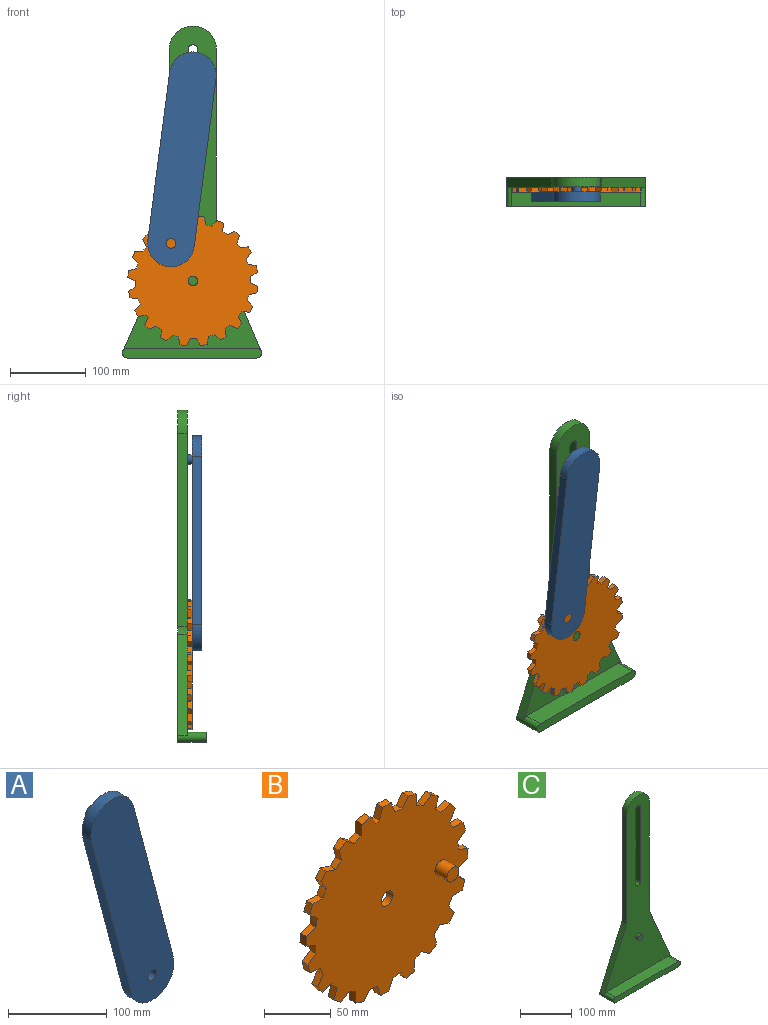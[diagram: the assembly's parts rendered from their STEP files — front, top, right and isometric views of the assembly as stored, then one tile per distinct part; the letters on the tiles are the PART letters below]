
ASSEMBLY  parts=3 mates=3
PART A: 9 faces, bbox 118.8x31.8x277.6 mm
  f0: plane 277.6x118.85mm, normal (0,-1,0), area 16641.5mm2, adj f1,f3,f4,f5,f6
  f1: plane 215.9x57.15mm, normal (0.97,0,0.26), area 2836.4mm2, adj f0,f2,f4,f5
  f2: plane 277.6x118.85mm, normal (0,1,0), area 16514.8mm2, adj f1,f3,f4,f5,f6,f8
  f3: cylinder r=6.35mm len=12.7mm, axis (0,1,0), area 506.7mm2, adj f0,f2
  f4: cylinder r=30.85mm len=60.67mm, axis (0,1,0), area 1230.8mm2, adj f0,f1,f2,f6
  f5: cylinder r=30.85mm len=60.67mm, axis (0,1,0), area 1230.8mm2, adj f0,f1,f2,f6
  f6: plane 215.9x57.15mm, normal (-0.97,0,-0.26), area 2836.4mm2, adj f0,f2,f4,f5
  f7: plane 12.7x12.7mm, normal (0,1,0), area 126.7mm2, adj f8
  f8: cylinder r=6.35mm len=19.05mm, axis (0,-1,0), area 760.1mm2, adj f2,f7
PART B: 85 faces, bbox 171.6x19.1x171.5 mm
  f0: plane 10.58x6.35mm, normal (0.05,0,1), area 67.2mm2, adj f1,f79,f80,f81
  f1: cylinder r=76.2mm len=7.18mm, axis (0,1,0), area 50.9mm2, adj f0,f2,f80,f81
  f2: plane 8.73x6.35mm, normal (0.82,0,-0.57), area 67.2mm2, adj f1,f3,f80,f81
  f3: plane 7.21x6.35mm, normal (0.81,0,0.58), area 56.2mm2, adj f2,f4,f80,f81
  f4: plane 10.2x6.35mm, normal (-0.27,0,0.96), area 67.2mm2, adj f3,f5,f80,f81
  f5: cylinder r=76.2mm len=6.35mm, axis (0,1,0), area 50.9mm2, adj f4,f6,f80,f81
  f6: plane 10.16x6.35mm, normal (0.96,0,-0.28), area 67.2mm2, adj f5,f7,f80,f81
  f7: plane 7.13x6.35mm, normal (0.59,0,0.81), area 56.2mm2, adj f6,f8,f80,f81
  f8: plane 8.81x6.35mm, normal (-0.55,0,0.83), area 67.2mm2, adj f7,f9,f80,f81
  f9: cylinder r=76.2mm len=7.13mm, axis (0,1,0), area 50.9mm2, adj f8,f10,f80,f81
  f10: plane 10.58x6.35mm, normal (1,0,0.03), area 67.2mm2, adj f9,f11,f80,f81
  f11: plane 8.41x6.35mm, normal (0.31,0,0.95), area 56.2mm2, adj f10,f12,f80,f81
  f12: plane 8.33x6.54mm, normal (-0.79,0,0.62), area 67.2mm2, adj f11,f13,f80,f81
  f13: cylinder r=76.2mm len=7.92mm, axis (0,1,0), area 50.9mm2, adj f12,f14,f80,f81
  f14: plane 9.95x6.35mm, normal (0.94,0,0.34), area 67.2mm2, adj f13,f15,f80,f81
  f15: plane 8.85x6.35mm, normal (0,0,1), area 56.2mm2, adj f14,f16,f80,f81
  f16: plane 9.95x6.35mm, normal (-0.94,0,0.34), area 67.2mm2, adj f15,f17,f80,f81
  f17: cylinder r=76.2mm len=6.35mm, axis (0,1,0), area 24.3mm2, adj f16,f18,f80,f81
  f18: plane 8.67x6.35mm, normal (0.82,0,0.57), area 67.2mm2, adj f17,f19,f80,f81
  f19: plane 8.55x6.35mm, normal (-0.26,0,0.97), area 56.2mm2, adj f18,f20,f80,f81
  f20: plane 10.55x6.35mm, normal (-1,0,0.09), area 67.2mm2, adj f19,f21,f80,f81
  f21: cylinder r=76.2mm len=7.32mm, axis (0,1,0), area 50.9mm2, adj f20,f22,f80,f81
  f22: plane 8.48x6.35mm, normal (0.6,0,0.8), area 67.2mm2, adj f21,f23,f80,f81
  f23: plane 7.41x6.35mm, normal (-0.55,0,0.84), area 56.2mm2, adj f22,f24,f80,f81
  f24: plane 10.31x6.35mm, normal (-0.97,0,-0.23), area 67.2mm2, adj f23,f25,f80,f81
  f25: cylinder r=76.2mm len=6.35mm, axis (0,1,0), area 50.9mm2, adj f24,f26,f80,f81
  f26: plane 10.03x6.35mm, normal (0.32,0,0.95), area 67.2mm2, adj f25,f27,f80,f81
  f27: plane 6.91x6.35mm, normal (-0.78,0,0.63), area 56.2mm2, adj f26,f28,f80,f81
  f28: plane 9.05x6.35mm, normal (-0.85,0,-0.52), area 67.2mm2, adj f27,f29,f80,f81
  f29: cylinder r=76.2mm len=6.97mm, axis (0,1,0), area 50.9mm2, adj f28,f30,f80,f81
  f30: plane 10.59x6.35mm, normal (0.01,0,1), area 67.2mm2, adj f29,f31,f80,f81
  f31: plane 8.29x6.35mm, normal (-0.94,0,0.35), area 56.2mm2, adj f30,f32,f80,f81
  f32: plane 8.05x6.88mm, normal (-0.65,0,-0.76), area 67.2mm2, adj f31,f33,f80,f81
  f33: cylinder r=76.2mm len=7.86mm, axis (0,1,0), area 50.9mm2, adj f32,f34,f80,f81
  f34: plane 10.09x6.35mm, normal (-0.3,0,0.95), area 67.2mm2, adj f33,f35,f80,f81
  f35: plane 8.85x6.35mm, normal (-1,0,0.04), area 56.2mm2, adj f34,f36,f80,f81
  f36: plane 9.79x6.35mm, normal (-0.38,0,-0.92), area 67.2mm2, adj f35,f37,f80,f81
  f37: cylinder r=76.2mm len=7.96mm, axis (0,1,0), area 50.9mm2, adj f36,f38,f80,f81
  f38: plane 8.59x6.35mm, normal (-0.58,0,0.81), area 67.2mm2, adj f37,f39,f80,f81
  f39: plane 8.52x6.35mm, normal (-0.96,0,-0.27), area 56.2mm2, adj f38,f40,f80,f81
  f40: plane 10.56x6.35mm, normal (-0.07,0,-1), area 67.2mm2, adj f39,f41,f80,f81
  f41: cylinder r=76.2mm len=7.28mm, axis (0,1,0), area 50.9mm2, adj f40,f42,f80,f81
  f42: plane 8.56x6.35mm, normal (-0.81,0,0.59), area 67.2mm2, adj f41,f43,f80,f81
  f43: plane 7.34x6.35mm, normal (-0.83,0,-0.56), area 56.2mm2, adj f42,f44,f80,f81
  f44: plane 10.28x6.35mm, normal (0.24,0,-0.97), area 67.2mm2, adj f43,f45,f80,f81
  f45: cylinder r=76.2mm len=6.35mm, axis (0,1,0), area 50.9mm2, adj f44,f46,f80,f81
  f46: plane 10.08x6.35mm, normal (-0.95,0,0.31), area 67.2mm2, adj f45,f47,f80,f81
  f47: plane 6.99x6.35mm, normal (-0.61,0,-0.79), area 56.2mm2, adj f46,f48,f80,f81
  f48: plane 8.97x6.35mm, normal (0.53,0,-0.85), area 67.2mm2, adj f47,f49,f80,f81
  f49: cylinder r=76.2mm len=7.03mm, axis (0,1,0), area 50.9mm2, adj f48,f50,f80,f81
  f50: plane 10.59x6.35mm, normal (-1,0,0), area 67.2mm2, adj f49,f51,f80,f81
  f51: plane 8.33x6.35mm, normal (-0.34,0,-0.94), area 56.2mm2, adj f50,f52,f80,f81
  f52: plane 8.14x6.77mm, normal (0.77,0,-0.64), area 67.2mm2, adj f51,f53,f80,f81
  f53: cylinder r=76.2mm len=7.88mm, axis (0,1,0), area 50.9mm2, adj f52,f54,f80,f81
  f54: plane 10.05x6.35mm, normal (-0.95,0,-0.32), area 67.2mm2, adj f53,f55,f80,f81
  f55: plane 8.85x6.35mm, normal (-0.03,0,-1), area 56.2mm2, adj f54,f56,f80,f81
  f56: plane 9.85x6.35mm, normal (0.93,0,-0.37), area 67.2mm2, adj f55,f57,f80,f81
  f57: cylinder r=76.2mm len=7.95mm, axis (0,1,0), area 50.9mm2, adj f56,f58,f80,f81
  f58: plane 8.5x6.35mm, normal (-0.8,0,-0.6), area 67.2mm2, adj f57,f59,f80,f81
  f59: plane 8.48x6.35mm, normal (0.29,0,-0.96), area 56.2mm2, adj f58,f60,f80,f81
  f60: plane 10.57x6.35mm, normal (1,0,-0.06), area 67.2mm2, adj f59,f61,f80,f81
  f61: cylinder r=76.2mm len=7.23mm, axis (0,1,0), area 50.9mm2, adj f60,f62,f80,f81
  f62: plane 8.65x6.35mm, normal (-0.58,0,-0.82), area 67.2mm2, adj f61,f63,f80,f81
  f63: plane 7.28x6.35mm, normal (0.57,0,-0.82), area 56.2mm2, adj f62,f64,f80,f81
  f64: plane 10.24x6.35mm, normal (0.97,0,0.25), area 67.2mm2, adj f63,f65,f80,f81
  f65: cylinder r=76.2mm len=6.35mm, axis (0,1,0), area 50.9mm2, adj f64,f66,f80,f81
  f66: plane 10.12x6.35mm, normal (-0.29,0,-0.96), area 67.2mm2, adj f65,f67,f80,f81
  f67: plane 7.06x6.35mm, normal (0.8,0,-0.6), area 56.2mm2, adj f66,f68,f80,f81
  f68: plane 8.89x6.35mm, normal (0.84,0,0.54), area 67.2mm2, adj f67,f69,f80,f81
  f69: cylinder r=76.2mm len=7.08mm, axis (0,1,0), area 50.9mm2, adj f68,f70,f80,f81
  f70: plane 10.59x6.35mm, normal (0.02,0,-1), area 67.2mm2, adj f69,f71,f80,f81
  f71: plane 8.37x6.35mm, normal (0.95,0,-0.32), area 56.2mm2, adj f70,f72,f80,f81
  f72: plane 8.24x6.66mm, normal (0.63,0,0.78), area 67.2mm2, adj f71,f73,f80,f81
  f73: cylinder r=76.2mm len=7.9mm, axis (0,1,0), area 50.9mm2, adj f72,f74,f80,f81
  f74: plane 10x6.35mm, normal (0.33,0,-0.94), area 67.2mm2, adj f73,f75,f80,f81
  f75: plane 8.85x6.35mm, normal (1,0,-0.01), area 56.2mm2, adj f74,f76,f80,f81
  f76: plane 9.9x6.35mm, normal (0.35,0,0.93), area 67.2mm2, adj f75,f77,f80,f81
  f77: cylinder r=76.2mm len=7.93mm, axis (0,1,0), area 50.9mm2, adj f76,f78,f80,f81
  f78: plane 8.42x6.43mm, normal (0.61,0,-0.79), area 67.2mm2, adj f77,f79,f80,f81
  f79: plane 8.45x6.35mm, normal (0.95,0,0.3), area 56.2mm2, adj f0,f78,f80,f81
  f80: plane 171.61x171.54mm, normal (0,-1,0), area 20379.4mm2, adj f0,f1,f2,f3,f4,f5,f6,f7
  f81: plane 171.61x171.54mm, normal (0,1,0), area 20506mm2, adj f0,f1,f2,f3,f4,f5,f6,f7
  f82: cylinder r=6.35mm len=12.7mm, axis (0,1,0), area 506.7mm2, adj f80,f83
  f83: plane 12.7x12.7mm, normal (0,-1,0), area 126.7mm2, adj f82
  f84: cylinder r=6.35mm len=12.7mm, axis (0,-1,0), area 253.4mm2, adj f80,f81
PART C: 20 faces, bbox 183.7x38.1x437.5 mm
  f0: plane 428.62x182.6mm, normal (0,-1,0), area 31354.2mm2, adj f1,f2,f3,f5,f6,f7,f8,f9
  f1: cylinder r=25.4mm len=12.7mm, axis (0,-1,0), area 134.7mm2, adj f0,f2,f14,f15
  f2: plane 133.36x59.16mm, normal (-0.91,0,0.41), area 1852.8mm2, adj f0,f1,f3,f15
  f3: cylinder r=6.35mm len=38.1mm, axis (0,-1,0), area 667.1mm2, adj f0,f2,f4,f15,f18,f19
  f4: plane 170.95x38.1mm, normal (0,0,-1), area 6513.3mm2, adj f3,f5,f15,f19
  f5: cylinder r=6.35mm len=38.1mm, axis (0,-1,0), area 666mm2, adj f0,f4,f6,f15,f18,f19
  f6: plane 133.57x57.08mm, normal (0.92,0,0.39), area 1844.8mm2, adj f0,f5,f7,f15
  f7: cylinder r=25.4mm len=12.7mm, axis (0,-1,0), area 130.3mm2, adj f0,f6,f8,f15
  f8: plane 254x12.7mm, normal (1,0,0), area 3225.8mm2, adj f0,f7,f9,f15
  f9: cylinder r=31.07mm len=62.13mm, axis (0,-1,0), area 1239.5mm2, adj f0,f8,f14,f15
  f10: cylinder r=6.35mm len=12.7mm, axis (0,-1,0), area 253.4mm2, adj f0,f11,f13,f15
  f11: plane 177.8x12.7mm, normal (1,0,0), area 2258.1mm2, adj f0,f10,f12,f15
  f12: cylinder r=6.35mm len=12.7mm, axis (0,-1,0), area 253.4mm2, adj f0,f11,f13,f15
  f13: plane 177.8x12.7mm, normal (-1,0,0), area 2258.1mm2, adj f0,f10,f12,f15
  f14: plane 253.82x12.7mm, normal (-1,0,0), area 3223.5mm2, adj f0,f1,f9,f15
  f15: plane 437.47x183.65mm, normal (0,1,0), area 33778.6mm2, adj f1,f2,f3,f4,f5,f6,f7,f8
  f16: cylinder r=6.35mm len=12.7mm, axis (0,1,0), area 253.4mm2, adj f0,f17
  f17: plane 12.7x12.7mm, normal (0,-1,0), area 126.7mm2, adj f16
  f18: plane 170.95x25.4mm, normal (0,0,1), area 4342.2mm2, adj f0,f3,f5,f19
  f19: plane 183.65x12.7mm, normal (0,-1,0), area 2297.8mm2, adj f3,f4,f5,f18
PLACE A rot(axis=(0,1,0),22.2deg) t=(-148.73,-35.21,142.94)mm
PLACE B rot(axis=(0,-1,0),120.2deg) t=(-67.06,-35.21,71.94)mm
PLACE C t=(-67.06,-35.21,71.94)mm fixed
MATE revolute C.f16 <-> B.f1  axis (0,1,0) through (-67.06,-38.38,71.94)mm
MATE pin_slot A.f4 <-> C.f9  axis (0,1,0) through (-67.06,-22.51,342.8)mm
MATE revolute B.f82 <-> A.f3  axis (0,1,0) through (-95.83,-47.91,121.32)mm
